# Revit family: Shower-Shower_Column_Kit-KOHLER-Fluence-K-38055T
name_source: partatom
category: Plumbing Fixtures
units: mm (PartAtom-declared; Revit-internal decimal feet)

## family parameters
Cut with Voids When Loaded = No
Host = Face
Maintain Annotation Orientation = No
OmniClass Number = 23.31.17.00
Part Type = Normal
Room Calculation Point = No
Round Connector Dimension = Use Diameter
Shared = No

## types (3) — shared parameters
ADA Compliant = No
Assembly Code = D2010700
CW Connection = Yes
Cold Water Inlet = Cold Water Inlet
Date Modified = 12/19/2024
Default Elevation = 72"
Description = Thermostatic 3-Way Shower Column Direct Connection
Drain Included = No
Flow Rate = 3 GPM
HW Connection = Yes
Handle Clearance = 3 1/2"
Height = 47 15/16"
Hot Water Inlet = Hot Water Inlet
Length = 23 1/8"
Manufacturer = Kohler Co.
Master Format 2014 = 22 42 23
Master Format 2014 Name = Residential Showers
Material = Premium Metal Construction
Pressure = 0.00 psi
Product Name = Fluence
URL = http://www.kohler.com.cn
Vent Connection = No
Waste Connection = No
Waste Water Outlet = Waste Water Outlet
WaterSense Certified = No
Width = 12 11/16"

## per-type parameters (varying)
| type | Finish | Handshower Nozzel Finish | Model | Secondary Finish | Type |
| CP-Polished Chrome | Kohler-Metal-CP-Polished_Chrome | Kohler-Plastic-0-White | K-38055T-9-CP | Kohler-Plastic-0-White | 1 |
| BL-Matte Black | Kohler-Metal-BL-Matte_Black | Plastic-Pantone-PQ-194205-TCX | K-38055T-9-BL | Kohler-Plastic-7-Black_Black | 2 |
| BN-Vibrant Brushed Nickel | Kohler-Metal-BN-Vibrant_Brushed_Nickel | Plastic-Pantone-PQ-194205-TCX | K-38055T-9-BN | Kohler-Plastic-Pantone-13-0000 TPG | 3 |

## geometry (parser evidence)
native form markers: Sweep x6
no freeform markers — native parametric forms only
